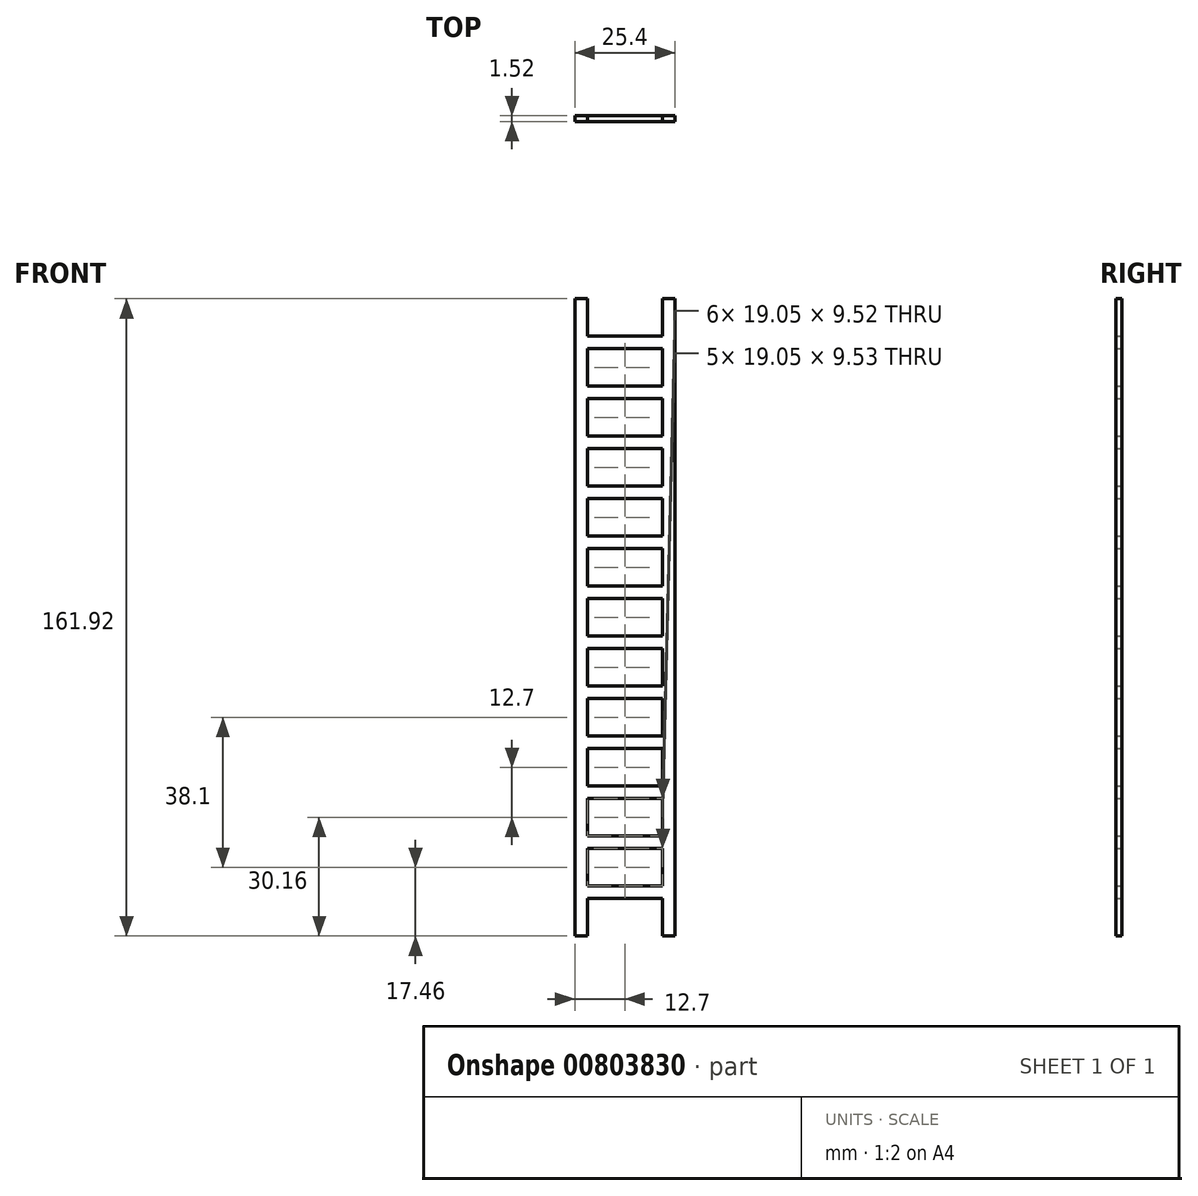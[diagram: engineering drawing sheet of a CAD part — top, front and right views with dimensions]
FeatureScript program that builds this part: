
annotation { "Feature Type Name" : "Feature", "Feature Type Description" : "" }
export const myFeature = defineFeature(function(context is Context, id is Id, definition is map)
    precondition{}
    {
        {
            var Q0;
            Q0=qCreatedBy(makeId("Front.planeOp"),FACE);
            var sketch = newSketch(context, id + "F0", { "sketchPlane" : qUnion([Q0])});
            skLineSegment(sketch, "E0.bottom", {"start": v(-12.7, 80.96) * mm, "end": v(12.7, 80.96) * mm});
            skLineSegment(sketch, "E0.top", {"start": v(-12.7, -80.96) * mm, "end": v(12.7, -80.96) * mm});
            skLineSegment(sketch, "E0.left", {"start": v(-12.7, 80.96) * mm, "end": v(-12.7, -80.96) * mm});
            skLineSegment(sketch, "E0.right", {"start": v(12.7, 80.96) * mm, "end": v(12.7, -80.96) * mm});
            skPoint(sketch, "E0.middle", {"position": v(0, 0) * mm});
            skLineSegment(sketch, "E1.bottom", {"start": v(-9.53, -71.44) * mm, "end": v(9.53, -71.44) * mm});
            skLineSegment(sketch, "E1.top", {"start": v(-9.53, -80.96) * mm, "end": v(9.52, -80.96) * mm});
            skLineSegment(sketch, "E1.left", {"start": v(-9.53, -71.44) * mm, "end": v(-9.53, -80.96) * mm});
            skLineSegment(sketch, "E1.right", {"start": v(9.52, -71.44) * mm, "end": v(9.52, -80.96) * mm});
            skPoint(sketch, "E1.middle", {"position": v(0, -76.2) * mm});
            skLineSegment(sketch, "E2.0.1.0", {"start": v(9.52, -58.74) * mm, "end": v(9.52, -68.26) * mm});
            skLineSegment(sketch, "E2.0.1.1", {"start": v(-9.53, -58.74) * mm, "end": v(-9.53, -68.26) * mm});
            skLineSegment(sketch, "E2.0.1.2", {"start": v(-9.53, -68.26) * mm, "end": v(9.52, -68.26) * mm});
            skPoint(sketch, "E2.0.1.3", {"position": v(0, -63.5) * mm});
            skLineSegment(sketch, "E2.0.1.4", {"start": v(-9.53, -58.74) * mm, "end": v(9.53, -58.74) * mm});
            skLineSegment(sketch, "E2.0.2.0", {"start": v(9.52, -46.04) * mm, "end": v(9.52, -55.56) * mm});
            skLineSegment(sketch, "E2.0.2.1", {"start": v(-9.53, -46.04) * mm, "end": v(-9.53, -55.56) * mm});
            skLineSegment(sketch, "E2.0.2.2", {"start": v(-9.53, -55.56) * mm, "end": v(9.52, -55.56) * mm});
            skPoint(sketch, "E2.0.2.3", {"position": v(0, -50.8) * mm});
            skLineSegment(sketch, "E2.0.2.4", {"start": v(-9.53, -46.04) * mm, "end": v(9.53, -46.04) * mm});
            skLineSegment(sketch, "E2.0.3.0", {"start": v(9.52, -33.34) * mm, "end": v(9.52, -42.86) * mm});
            skLineSegment(sketch, "E2.0.3.1", {"start": v(-9.53, -33.34) * mm, "end": v(-9.53, -42.86) * mm});
            skLineSegment(sketch, "E2.0.3.2", {"start": v(-9.53, -42.86) * mm, "end": v(9.52, -42.86) * mm});
            skPoint(sketch, "E2.0.3.3", {"position": v(0, -38.1) * mm});
            skLineSegment(sketch, "E2.0.3.4", {"start": v(-9.53, -33.34) * mm, "end": v(9.53, -33.34) * mm});
            skLineSegment(sketch, "E2.0.4.0", {"start": v(9.52, -20.64) * mm, "end": v(9.52, -30.16) * mm});
            skLineSegment(sketch, "E2.0.4.1", {"start": v(-9.53, -20.64) * mm, "end": v(-9.53, -30.16) * mm});
            skLineSegment(sketch, "E2.0.4.2", {"start": v(-9.53, -30.16) * mm, "end": v(9.52, -30.16) * mm});
            skPoint(sketch, "E2.0.4.3", {"position": v(0, -25.4) * mm});
            skLineSegment(sketch, "E2.0.4.4", {"start": v(-9.53, -20.64) * mm, "end": v(9.53, -20.64) * mm});
            skLineSegment(sketch, "E2.direction1", {"start": v(-9.52, -80.96) * mm, "end": v(15.88, -80.96) * mm, "construction": true});
            skLineSegment(sketch, "E2.direction2", {"start": v(-9.53, -80.96) * mm, "end": v(-9.53, -68.26) * mm, "construction": true});
            skLineSegment(sketch, "E3.bottom", {"start": v(9.53, 4.76) * mm, "end": v(-9.53, 4.76) * mm});
            skLineSegment(sketch, "E4.0.0.5", {"start": v(9.52, -7.94) * mm, "end": v(9.52, -17.46) * mm});
            skLineSegment(sketch, "E4.3.0.5", {"start": v(-9.53, -7.94) * mm, "end": v(-9.53, -17.46) * mm});
            skLineSegment(sketch, "E4.6.0.5", {"start": v(-9.53, -17.46) * mm, "end": v(9.52, -17.46) * mm});
            skPoint(sketch, "E4.9.0.5", {"position": v(0, -12.7) * mm});
            skLineSegment(sketch, "E4.10.0.5", {"start": v(-9.53, -7.94) * mm, "end": v(9.53, -7.94) * mm});
            skLineSegment(sketch, "E4.0.0.6", {"start": v(9.52, 4.76) * mm, "end": v(9.52, -4.76) * mm});
            skLineSegment(sketch, "E4.3.0.6", {"start": v(-9.53, 4.76) * mm, "end": v(-9.53, -4.76) * mm});
            skLineSegment(sketch, "E4.6.0.6", {"start": v(-9.53, -4.76) * mm, "end": v(9.52, -4.76) * mm});
            skLineSegment(sketch, "E4.10.0.6", {"start": v(-9.53, 4.76) * mm, "end": v(9.53, 4.76) * mm});
            skLineSegment(sketch, "E4.0.0.7", {"start": v(9.52, 17.46) * mm, "end": v(9.52, 7.94) * mm});
            skLineSegment(sketch, "E4.3.0.7", {"start": v(-9.53, 17.46) * mm, "end": v(-9.53, 7.94) * mm});
            skLineSegment(sketch, "E4.6.0.7", {"start": v(-9.53, 7.94) * mm, "end": v(9.52, 7.94) * mm});
            skPoint(sketch, "E4.9.0.7", {"position": v(0, 12.7) * mm});
            skLineSegment(sketch, "E4.10.0.7", {"start": v(-9.53, 17.46) * mm, "end": v(9.53, 17.46) * mm});
            skLineSegment(sketch, "E4.0.0.8", {"start": v(9.52, 30.16) * mm, "end": v(9.52, 20.64) * mm});
            skLineSegment(sketch, "E4.3.0.8", {"start": v(-9.53, 30.16) * mm, "end": v(-9.53, 20.64) * mm});
            skLineSegment(sketch, "E4.6.0.8", {"start": v(-9.53, 20.64) * mm, "end": v(9.52, 20.64) * mm});
            skPoint(sketch, "E4.9.0.8", {"position": v(0, 25.4) * mm});
            skLineSegment(sketch, "E4.10.0.8", {"start": v(-9.53, 30.16) * mm, "end": v(9.53, 30.16) * mm});
            skLineSegment(sketch, "E4.0.0.9", {"start": v(9.52, 42.86) * mm, "end": v(9.52, 33.34) * mm});
            skLineSegment(sketch, "E4.3.0.9", {"start": v(-9.53, 42.86) * mm, "end": v(-9.53, 33.34) * mm});
            skLineSegment(sketch, "E4.6.0.9", {"start": v(-9.53, 33.34) * mm, "end": v(9.52, 33.34) * mm});
            skPoint(sketch, "E4.9.0.9", {"position": v(0, 38.1) * mm});
            skLineSegment(sketch, "E4.10.0.9", {"start": v(-9.53, 42.86) * mm, "end": v(9.53, 42.86) * mm});
            skLineSegment(sketch, "E4.0.0.10", {"start": v(9.52, 55.56) * mm, "end": v(9.52, 46.04) * mm});
            skLineSegment(sketch, "E4.3.0.10", {"start": v(-9.53, 55.56) * mm, "end": v(-9.53, 46.04) * mm});
            skLineSegment(sketch, "E4.6.0.10", {"start": v(-9.53, 46.04) * mm, "end": v(9.52, 46.04) * mm});
            skPoint(sketch, "E4.9.0.10", {"position": v(0, 50.8) * mm});
            skLineSegment(sketch, "E4.10.0.10", {"start": v(-9.53, 55.56) * mm, "end": v(9.53, 55.56) * mm});
            skLineSegment(sketch, "E4.0.0.11", {"start": v(9.52, 68.26) * mm, "end": v(9.52, 58.74) * mm});
            skLineSegment(sketch, "E4.3.0.11", {"start": v(-9.53, 68.26) * mm, "end": v(-9.53, 58.74) * mm});
            skLineSegment(sketch, "E4.6.0.11", {"start": v(-9.53, 58.74) * mm, "end": v(9.52, 58.74) * mm});
            skPoint(sketch, "E4.9.0.11", {"position": v(0, 63.5) * mm});
            skLineSegment(sketch, "E4.10.0.11", {"start": v(-9.53, 68.26) * mm, "end": v(9.53, 68.26) * mm});
            skLineSegment(sketch, "E4.0.0.12", {"start": v(9.52, 80.96) * mm, "end": v(9.52, 71.44) * mm});
            skLineSegment(sketch, "E4.3.0.12", {"start": v(-9.53, 80.96) * mm, "end": v(-9.53, 71.44) * mm});
            skLineSegment(sketch, "E4.6.0.12", {"start": v(-9.53, 71.44) * mm, "end": v(9.52, 71.44) * mm});
            skPoint(sketch, "E4.9.0.12", {"position": v(0, 76.2) * mm});
            skLineSegment(sketch, "E4.10.0.12", {"start": v(-9.53, 80.96) * mm, "end": v(9.53, 80.96) * mm});
            skSolve(sketch);
        }
        {
            var Q0;
            {var subQ4=sQuery(id+"F0.wireOp",EDGE,"E0.left");Q0=makeQuery(id+"F0.imprint","IMPRINT",FACE,{"disambiguationData":[TD([[makeQuery(id+"F0.imprint","IMPRINT",EDGE,{"derivedFrom":subQ4}),1.0]])]});}
            extrude(context, id + "F1", {"entities" : qUnion([Q0]), "depth" : 1.52 * mm, "offsetDistance" : 25.4 * mm});
        }
    });
